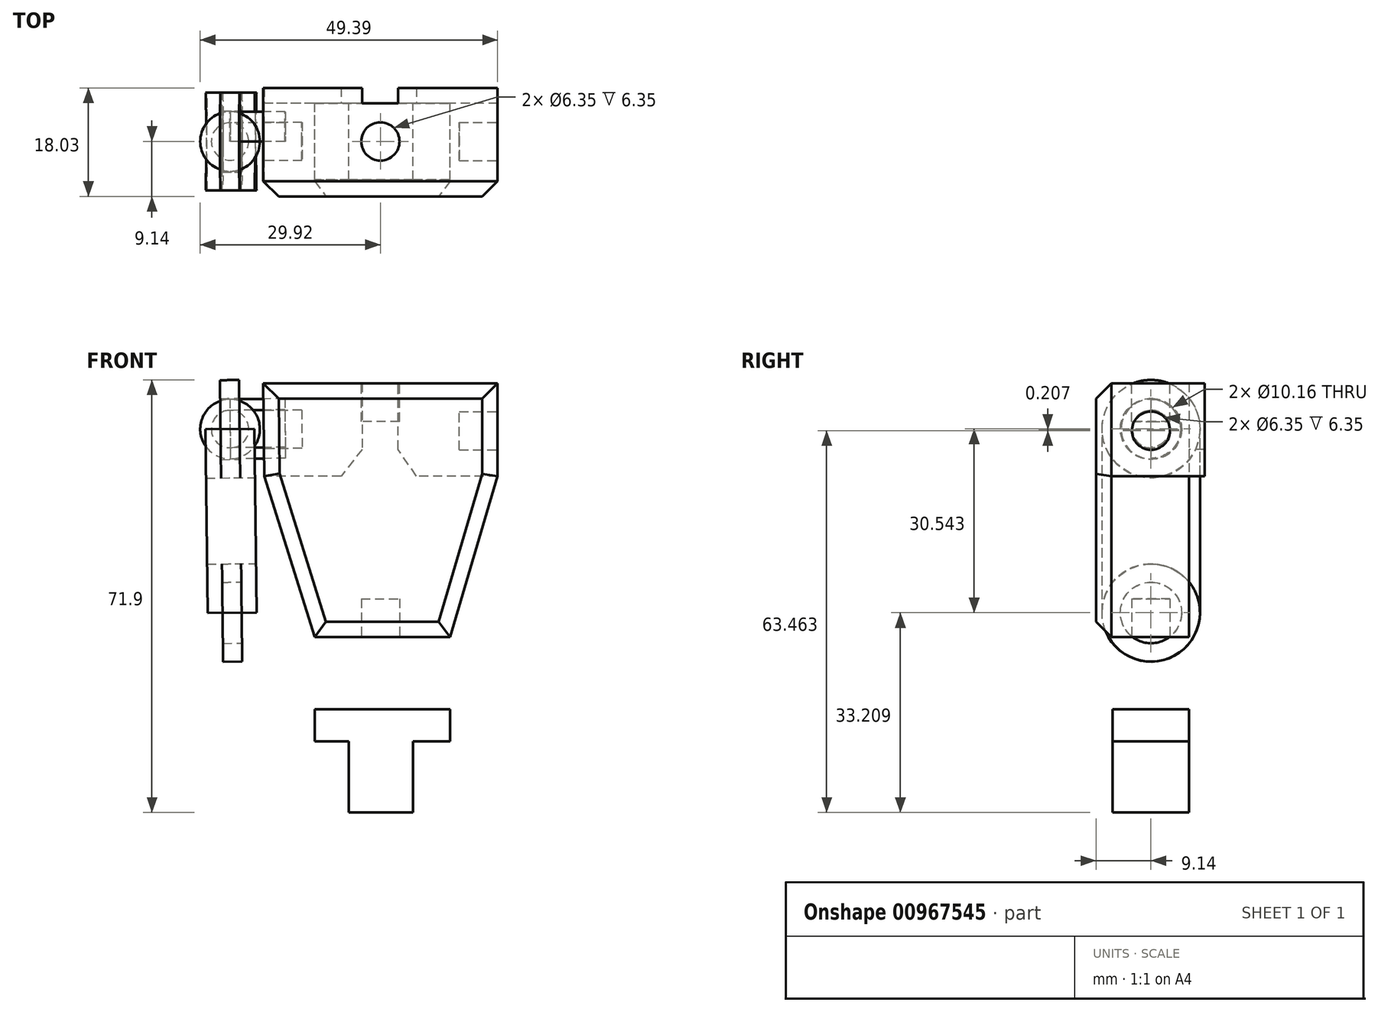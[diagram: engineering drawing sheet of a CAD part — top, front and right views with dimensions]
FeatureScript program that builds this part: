
annotation { "Feature Type Name" : "Feature", "Feature Type Description" : "" }
export const myFeature = defineFeature(function(context is Context, id is Id, definition is map)
    precondition{}
    {
        {
            var Q0;
            Q0=qCreatedBy(makeId("Front.planeOp"),FACE);
            var sketch = newSketch(context, id + "F0", { "sketchPlane" : qUnion([Q0])});
            skLineSegment(sketch, "E0", {"start": v(-19.47, 46.82) * mm, "end": v(19.47, 46.82) * mm});
            skLineSegment(sketch, "E1", {"start": v(19.47, 46.82) * mm, "end": v(19.47, 31.39) * mm});
            skLineSegment(sketch, "E2", {"start": v(19.47, 31.39) * mm, "end": v(11.58, 4.63) * mm});
            skLineSegment(sketch, "E3", {"start": v(11.58, 4.63) * mm, "end": v(-10.9, 4.63) * mm});
            skLineSegment(sketch, "E4", {"start": v(-10.9, 4.63) * mm, "end": v(-19.3, 31.39) * mm});
            skLineSegment(sketch, "E5", {"start": v(-19.3, 31.39) * mm, "end": v(-19.47, 46.82) * mm});
            skLineSegment(sketch, "E6", {"start": v(-10.9, -7.37) * mm, "end": v(11.58, -7.37) * mm});
            skLineSegment(sketch, "E7", {"start": v(11.58, -7.37) * mm, "end": v(11.58, -12.7) * mm});
            skLineSegment(sketch, "E8", {"start": v(11.58, -12.7) * mm, "end": v(5.4, -12.7) * mm});
            skLineSegment(sketch, "E9", {"start": v(5.4, -12.7) * mm, "end": v(5.4, -24.53) * mm});
            skLineSegment(sketch, "E10", {"start": v(5.4, -24.53) * mm, "end": v(-5.23, -24.53) * mm});
            skLineSegment(sketch, "E11", {"start": v(-5.23, -24.53) * mm, "end": v(-5.23, -12.7) * mm});
            skLineSegment(sketch, "E12", {"start": v(-5.23, -12.7) * mm, "end": v(-10.9, -12.7) * mm});
            skLineSegment(sketch, "E13", {"start": v(-10.9, -12.7) * mm, "end": v(-10.9, -7.37) * mm});
            skSolve(sketch);
        }
        {
            var Q0;
            Q0=makeQuery(id+"F0.imprint","IMPRINT",FACE,{"disambiguationData":[TD([[makeQuery(id+"F0.imprint","IMPRINT",EDGE,{"derivedFrom":sQuery(id+"F0.wireOp",EDGE,"E0")}),-1.0]])]});
            var Q1;
            Q1=makeQuery(id+"F0.imprint","IMPRINT",FACE,{"disambiguationData":[TD([[makeQuery(id+"F0.imprint","IMPRINT",EDGE,{"derivedFrom":sQuery(id+"F0.wireOp",EDGE,"E6")}),-1.0]])]});
            extrude(context, id + "F1", {"entities" : qUnion([Q0, Q1]), "depth" : 12.7 * mm, "offsetDistance" : 25.4 * mm, "symmetric" : true});
        }
        {
            var Q0;
            Q0=makeQuery(id+"F1.opExtrude","SWEPT_FACE",FACE,{"disambiguationData":[OSD([sQuery(id+"F0.wireOp",EDGE,"E5")])]});
            var sketch = newSketch(context, id + "F2", { "sketchPlane" : qUnion([Q0])});
            skCircle(sketch, "E14", {"center": v(0, 39.32) * mm, "radius": 3.18 * mm});
            skSolve(sketch);
        }
        {
            var Q0;
            Q0=makeQuery(id+"F2.imprint","IMPRINT",FACE,{"disambiguationData":[TD([[makeQuery(id+"F2.imprint","IMPRINT",EDGE,{"derivedFrom":sQuery(id+"F2.wireOp",EDGE,"E14")}),1.0]])]});
            extrude(context, id + "F3", {"entities" : qUnion([Q0]), "operationType" : NewBodyOperationType.REMOVE, "oppositeDirection" : true, "depth" : 6.35 * mm, "offsetDistance" : 25.4 * mm});
        }
        {
            var Q0;
            Q0=makeQuery(id+"F1.opExtrude","SWEPT_FACE",FACE,{"disambiguationData":[OSD([sQuery(id+"F0.wireOp",EDGE,"E1")])]});
            var sketch = newSketch(context, id + "F4", { "sketchPlane" : qUnion([Q0])});
            skCircle(sketch, "E15", {"center": v(0, 38.93) * mm, "radius": 3.18 * mm});
            skSolve(sketch);
        }
        {
            var Q0;
            Q0 = qSketchRegion(id + "F4", true);
            extrude(context, id + "F5", {"entities" : qUnion([Q0]), "operationType" : NewBodyOperationType.REMOVE, "oppositeDirection" : true, "depth" : 6.35 * mm, "offsetDistance" : 25.4 * mm});
        }
        {
            var Q0;
            Q0=makeQuery(id+"F1.opExtrude","SWEPT_FACE",FACE,{"disambiguationData":[OSD([sQuery(id+"F0.wireOp",EDGE,"E0")])]});
            var sketch = newSketch(context, id + "F6", { "sketchPlane" : qUnion([Q0])});
            skCircle(sketch, "E16", {"center": v(0, 0) * mm, "radius": 3.18 * mm});
            skSolve(sketch);
        }
        {
            var Q0;
            Q0=makeQuery(id+"F6.imprint","IMPRINT",FACE,{"disambiguationData":[TD([[makeQuery(id+"F6.imprint","IMPRINT",EDGE,{"derivedFrom":sQuery(id+"F6.wireOp",EDGE,"E16")}),1.0]])]});
            extrude(context, id + "F7", {"entities" : qUnion([Q0]), "operationType" : NewBodyOperationType.REMOVE, "oppositeDirection" : true, "depth" : 6.35 * mm, "offsetDistance" : 25.4 * mm});
        }
        {
            var Q0;
            Q0=makeQuery(id+"F1.opExtrude","SWEPT_FACE",FACE,{"disambiguationData":[OSD([sQuery(id+"F0.wireOp",EDGE,"E3")])]});
            var sketch = newSketch(context, id + "F8", { "sketchPlane" : qUnion([Q0])});
            skCircle(sketch, "E17", {"center": v(0, 0) * mm, "radius": 3.18 * mm});
            skSolve(sketch);
        }
        {
            var Q0;
            Q0=makeQuery(id+"F8.imprint","IMPRINT",FACE,{"disambiguationData":[TD([[makeQuery(id+"F8.imprint","IMPRINT",EDGE,{"derivedFrom":sQuery(id+"F8.wireOp",EDGE,"E17")}),1.0]])]});
            extrude(context, id + "F9", {"entities" : qUnion([Q0]), "operationType" : NewBodyOperationType.REMOVE, "oppositeDirection" : true, "depth" : 6.35 * mm, "offsetDistance" : 25.4 * mm});
        }
        {
            var Q0;
            Q0=makeQuery(id+"F1.opExtrude","CAP_FACE",FACE,{"disambiguationData":[OSD([sQuery(id+"F0.wireOp",EDGE,"E0"),sQuery(id+"F0.wireOp",EDGE,"E1"),sQuery(id+"F0.wireOp",EDGE,"E2"),sQuery(id+"F0.wireOp",EDGE,"E3"),sQuery(id+"F0.wireOp",EDGE,"E4"),sQuery(id+"F0.wireOp",EDGE,"E5")])],"isStart":false});
            var sketch = newSketch(context, id + "F10", { "sketchPlane" : qUnion([Q0])});
            skSolve(sketch);
        }
        {
            var Q0;
            Q0=makeQuery(id+"F10.imprint","IMPRINT",FACE,{"disambiguationData":[TD([[makeQuery(id+"F10.imprint","IMPRINT",EDGE,{"derivedFrom":makeQuery(id+"F1.opExtrude","CAP_EDGE",EDGE,{"disambiguationData":[OSD([sQuery(id+"F0.wireOp",EDGE,"E0")])],"isStart":false})}),-1.0]])]});
            extrude(context, id + "F11", {"entities" : qUnion([Q0]), "operationType" : NewBodyOperationType.ADD, "depth" : 2.8 * mm, "offsetDistance" : 25.4 * mm});
        }
        {
            var Q0;
            Q0=makeQuery(id+"F11.opExtrude","CAP_EDGE",EDGE,{"disambiguationData":[OSD([sQuery(id+"F0.wireOp",EDGE,"E5")])],"isStart":false});
            var Q1;
            Q1=makeQuery(id+"F11.opExtrude","CAP_EDGE",EDGE,{"disambiguationData":[OSD([sQuery(id+"F0.wireOp",EDGE,"E1")])],"isStart":false});
            var Q2;
            Q2=makeQuery(id+"F11.opExtrude","CAP_EDGE",EDGE,{"disambiguationData":[OSD([sQuery(id+"F0.wireOp",EDGE,"E0")])],"isStart":false});
            var Q3;
            Q3=makeQuery(id+"F11.opExtrude","CAP_EDGE",EDGE,{"disambiguationData":[OSD([sQuery(id+"F0.wireOp",EDGE,"E3")])],"isStart":false});
            var Q4;
            Q4=makeQuery(id+"F11.opExtrude","CAP_EDGE",EDGE,{"disambiguationData":[OSD([sQuery(id+"F0.wireOp",EDGE,"E4")])],"isStart":false});
            var Q5;
            Q5=makeQuery(id+"F11.opExtrude","CAP_EDGE",EDGE,{"disambiguationData":[OSD([sQuery(id+"F0.wireOp",EDGE,"E2")])],"isStart":false});
            chamfer(context, id + "F12", {"entities" : qUnion([Q0, Q1, Q2, Q3, Q4, Q5]), "width" : 2.54 * mm, "tangentPropagation" : true});
        }
        {
            var Q0;
            Q0=makeQuery(id+"F1.opExtrude","CAP_FACE",FACE,{"disambiguationData":[OSD([sQuery(id+"F0.wireOp",EDGE,"E0"),sQuery(id+"F0.wireOp",EDGE,"E1"),sQuery(id+"F0.wireOp",EDGE,"E2"),sQuery(id+"F0.wireOp",EDGE,"E3"),sQuery(id+"F0.wireOp",EDGE,"E4"),sQuery(id+"F0.wireOp",EDGE,"E5")])],"isStart":true});
            var sketch = newSketch(context, id + "F13", { "sketchPlane" : qUnion([Q0])});
            skLineSegment(sketch, "E18", {"start": v(-19.47, 31.39) * mm, "end": v(-6, 31.39) * mm});
            skLineSegment(sketch, "E19", {"start": v(-6, 31.39) * mm, "end": v(-2.92, 35.84) * mm});
            skLineSegment(sketch, "E20", {"start": v(-2.92, 35.84) * mm, "end": v(-2.92, 46.82) * mm});
            skLineSegment(sketch, "E21", {"start": v(-2.92, 46.82) * mm, "end": v(-19.47, 46.82) * mm});
            skLineSegment(sketch, "E22", {"start": v(-19.47, 46.82) * mm, "end": v(-19.47, 31.39) * mm});
            skLineSegment(sketch, "E23", {"start": v(3.03, 46.82) * mm, "end": v(3.03, 35.84) * mm});
            skLineSegment(sketch, "E24", {"start": v(3.03, 35.84) * mm, "end": v(6.52, 31.39) * mm});
            skLineSegment(sketch, "E25", {"start": v(6.52, 31.39) * mm, "end": v(19.3, 31.39) * mm});
            skLineSegment(sketch, "E26", {"start": v(19.3, 31.39) * mm, "end": v(19.47, 46.82) * mm});
            skLineSegment(sketch, "E27", {"start": v(19.47, 46.82) * mm, "end": v(3.03, 46.82) * mm});
            skSolve(sketch);
        }
        {
            var Q0;
            Q0=makeQuery(id+"F13.imprint","IMPRINT",FACE,{"disambiguationData":[TD([[makeQuery(id+"F13.imprint","IMPRINT",EDGE,{"derivedFrom":sQuery(id+"F13.wireOp",EDGE,"E18")}),1.0]])]});
            var Q1;
            Q1=makeQuery(id+"F13.imprint","IMPRINT",FACE,{"disambiguationData":[TD([[makeQuery(id+"F13.imprint","IMPRINT",EDGE,{"derivedFrom":sQuery(id+"F13.wireOp",EDGE,"E23")}),1.0]])]});
            extrude(context, id + "F14", {"entities" : qUnion([Q0, Q1]), "operationType" : NewBodyOperationType.ADD, "depth" : 2.54 * mm, "offsetDistance" : 25.4 * mm});
        }
        {
            var Q0;
            {var subQ0=sQuery(id+"F0.wireOp",EDGE,"E5");Q0=makeQuery(id+"F14.boolean.opBoolean","MERGE",FACE,{"derivedFrom":[makeQuery(id+"F11.boolean.opBoolean","MERGE",FACE,{"derivedFrom":[makeQuery(id+"F1.opExtrude","SWEPT_FACE",FACE,{"disambiguationData":[OSD([subQ0])]}),makeQuery(id+"F11.opExtrude","SWEPT_FACE",FACE,{"disambiguationData":[OSD([subQ0])]})]}),makeQuery(id+"F14.opExtrude","SWEPT_FACE",FACE,{"disambiguationData":[OSD([sQuery(id+"F13.wireOp",EDGE,"E26")])]})]});}
            cPlane(context, id + "F15", {"entities" : qUnion([Q0]), "cplaneType" : CPlaneType.OFFSET, "offset" : 5.6 * mm, "width" : 152.4 * mm, "height" : 152.4 * mm});
        }
        {
            var Q0;
            Q0=qCreatedBy(id+"F15.planeOp",FACE);
            var sketch = newSketch(context, id + "F16", { "sketchPlane" : qUnion([Q0])});
            skCircle(sketch, "E28", {"center": v(0, 39.5) * mm, "radius": 8.13 * mm});
            skCircle(sketch, "E29", {"center": v(0, 39.5) * mm, "radius": 5.08 * mm});
            skCircle(sketch, "E30", {"center": v(0, 8.95) * mm, "radius": 5.08 * mm});
            skCircle(sketch, "E31", {"center": v(0, 8.95) * mm, "radius": 8.13 * mm});
            skLineSegment(sketch, "E32", {"start": v(-8.13, 8.95) * mm, "end": v(-8.13, 39.5) * mm});
            skLineSegment(sketch, "E33", {"start": v(8.13, 8.95) * mm, "end": v(8.13, 39.5) * mm});
            skLineSegment(sketch, "E34", {"start": v(-5.08, 39.5) * mm, "end": v(-8.13, 39.5) * mm});
            skLineSegment(sketch, "E35", {"start": v(5.08, 39.5) * mm, "end": v(8.13, 39.5) * mm});
            skLineSegment(sketch, "E36", {"start": v(5.08, 8.95) * mm, "end": v(8.13, 8.95) * mm});
            skLineSegment(sketch, "E37", {"start": v(-5.08, 8.95) * mm, "end": v(-8.13, 8.95) * mm});
            skSolve(sketch);
        }
        {
            var Q0;
            {var subQ0=sQuery(id+"F16.wireOp",EDGE,"E34");Q0=makeQuery(id+"F16.imprint","IMPRINT",FACE,{"disambiguationData":[TD([[makeQuery(id+"F16.imprint","IMPRINT",EDGE,{"derivedFrom":subQ0}),-1.0]])]});}
            var Q1;
            {var subQ0=sQuery(id+"F16.wireOp",EDGE,"E36");Q1=makeQuery(id+"F16.imprint","IMPRINT",FACE,{"disambiguationData":[TD([[makeQuery(id+"F16.imprint","IMPRINT",EDGE,{"derivedFrom":subQ0}),-1.0]])]});}
            var Q2;
            {var subQ0=sQuery(id+"F16.wireOp",EDGE,"E34");Q2=makeQuery(id+"F16.imprint","IMPRINT",FACE,{"disambiguationData":[TD([[makeQuery(id+"F16.imprint","IMPRINT",EDGE,{"derivedFrom":subQ0}),1.0]])]});}
            var Q3;
            {var subQ0=sQuery(id+"F16.wireOp",EDGE,"E36");Q3=makeQuery(id+"F16.imprint","IMPRINT",FACE,{"disambiguationData":[TD([[makeQuery(id+"F16.imprint","IMPRINT",EDGE,{"derivedFrom":subQ0}),1.0]])]});}
            extrude(context, id + "F17", {"entities" : qUnion([Q0, Q1, Q2, Q3]), "operationType" : NewBodyOperationType.ADD, "depth" : 3.17 * mm, "offsetDistance" : 25.4 * mm, "symmetric" : true});
        }
        {
            var Q0;
            {var subQ0=sQuery(id+"F16.wireOp",EDGE,"E32");Q0=makeQuery(id+"F16.imprint","IMPRINT",FACE,{"disambiguationData":[TD([[makeQuery(id+"F16.imprint","IMPRINT",EDGE,{"derivedFrom":subQ0}),-1.0]])]});}
            extrude(context, id + "F18", {"entities" : qUnion([Q0]), "depth" : 8.13 * mm, "offsetDistance" : 25.4 * mm, "symmetric" : true});
        }
        {
            var Q0;
            Q0=qCreatedBy(id+"F15.planeOp",FACE);
            var sketch = newSketch(context, id + "F19", { "sketchPlane" : qUnion([Q0])});
            skArc(sketch, "E38", {"start": v(0, 44.44) * mm, "mid": v(-4.95, 39.48) * mm, "end": v(0, 34.53) * mm});
            skLineSegment(sketch, "E39", {"start": v(0, 44.44) * mm, "end": v(0, 34.53) * mm});
            skCircle(sketch, "E40", {"center": v(0, 39.48) * mm, "radius": 3.1 * mm});
            skSolve(sketch);
        }
        {
            var Q0;
            Q0=makeQuery(id+"F19.imprint","IMPRINT",FACE,{"disambiguationData":[TD([[makeQuery(id+"F19.imprint","IMPRINT",EDGE,{"derivedFrom":sQuery(id+"F19.wireOp",EDGE,"E38")}),1.0]])]});
            var Q1;
            Q1=sQuery(id+"F19.wireOp",EDGE,"E39");
            revolve(context, id + "F20", {"surfaceOperationType" : NewSurfaceOperationType.NEW, "entities" : qUnion([Q0]), "axis" : qUnion([Q1]), "revolveType" : RevolveType.FULL});
        }
        {
            var Q0;
            {var subQ0=sQuery(id+"F19.wireOp",EDGE,"E40");var subQ1=sQuery(id+"F19.wireOp",EDGE,"E39");var subQ2=makeQuery(id+"F19.imprint","INTERSECT",VERTEX,{"disambiguationData":[OD(0.0)],"derivedFrom":[subQ1,subQ0]});Q0=makeQuery(id+"F19.imprint","IMPRINT",FACE,{"disambiguationData":[TD([[makeQuery(id+"F19.imprint","IMPRINT",EDGE,{"disambiguationData":[TD([[subQ2,-1.0]])],"derivedFrom":subQ1}),1.0]])]});}
            var Q1;
            {var subQ0=sQuery(id+"F19.wireOp",EDGE,"E40");var subQ1=sQuery(id+"F19.wireOp",EDGE,"E39");var subQ2=makeQuery(id+"F19.imprint","INTERSECT",VERTEX,{"disambiguationData":[OD(0.0)],"derivedFrom":[subQ1,subQ0]});Q1=makeQuery(id+"F19.imprint","IMPRINT",FACE,{"disambiguationData":[TD([[makeQuery(id+"F19.imprint","IMPRINT",EDGE,{"disambiguationData":[TD([[subQ2,-1.0]])],"derivedFrom":subQ1}),-1.0]])]});}
            extrude(context, id + "F21", {"entities" : qUnion([Q0, Q1]), "oppositeDirection" : true, "depth" : 9.14 * mm, "offsetDistance" : 25.4 * mm});
        }
    });
